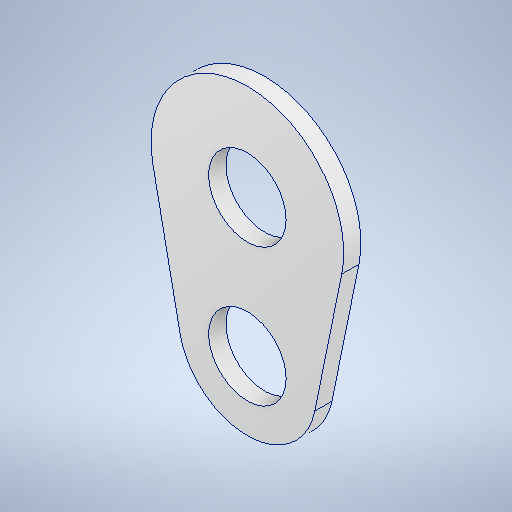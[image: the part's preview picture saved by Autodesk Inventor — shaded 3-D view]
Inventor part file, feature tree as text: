
AUTODESK INVENTOR PART (.ipt)
format: ipt  version: 2025.1 (Build 291241020, 241B)  size: 260,096 bytes
history: native  units: in
note: dims shown in document units (in); Inventor stores cm internally (conversion verified against a paired STEP export)
features: extrude x1, sketch x1
ambient origin geometry x8: Origin, YZ Plane, XZ Plane, XY Plane, X Axis, Y Axis, Z Axis, Center Point
bodies: Solid1 (feature_tree)
feature tree (2):
  extrude  "Extrusion1"  Depth=0.25in
  sketch  "Sketch1"  dims[d0=1.125in d2=1.6in d6=2.4in d7=1.125in d9=0.2in d10=0.2in d11=0.25in d12=0.0in]
